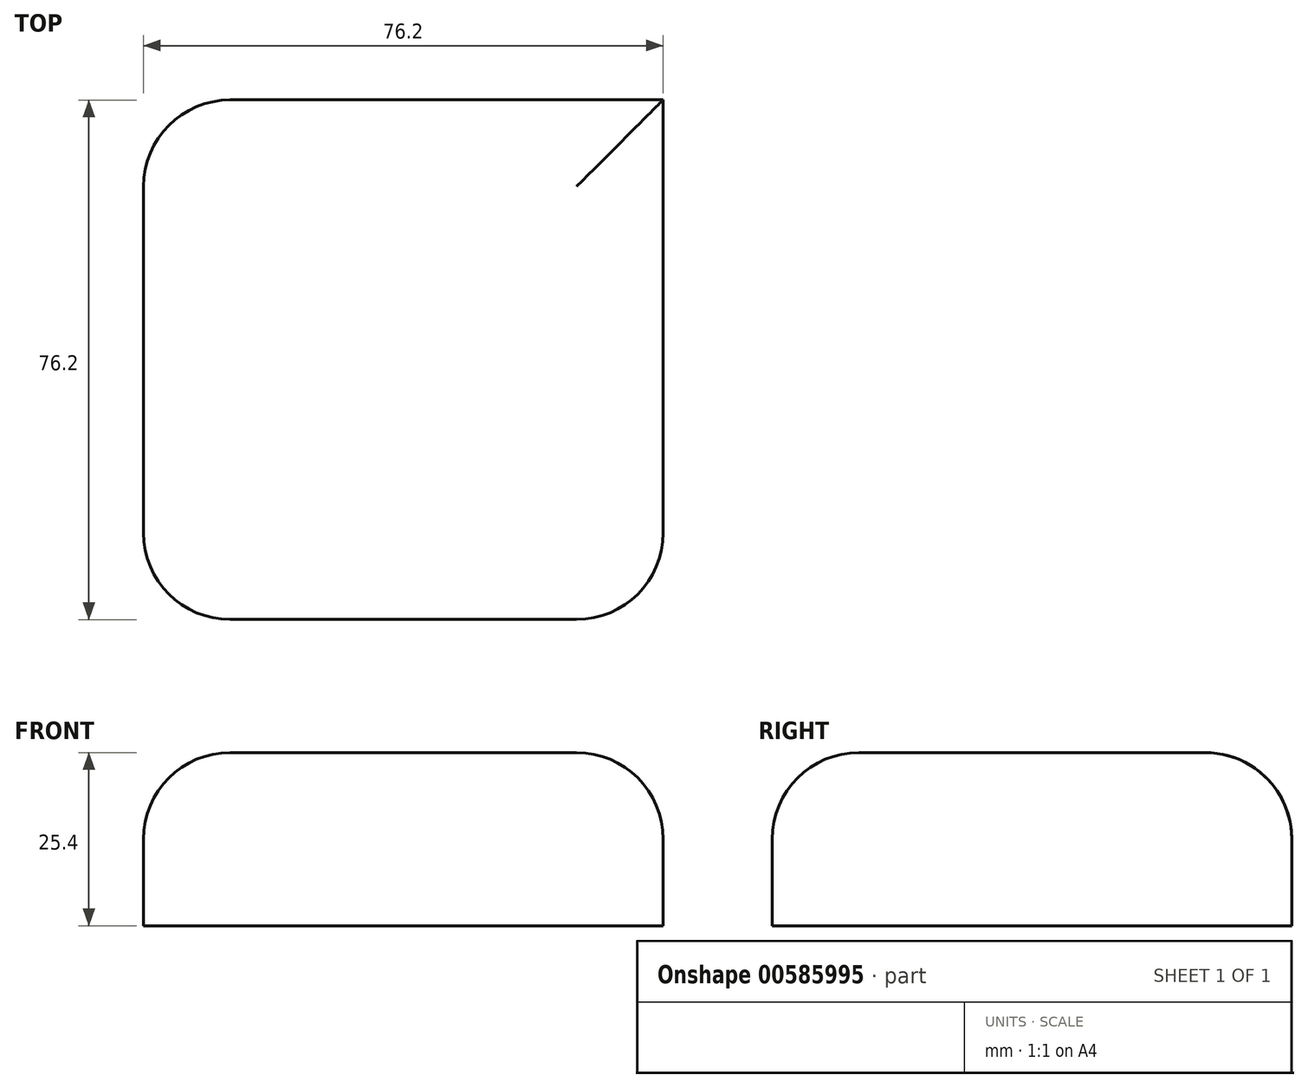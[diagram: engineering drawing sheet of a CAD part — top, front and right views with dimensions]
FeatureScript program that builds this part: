
annotation { "Feature Type Name" : "Feature", "Feature Type Description" : "" }
export const myFeature = defineFeature(function(context is Context, id is Id, definition is map)
    precondition{}
    {
        {
            var Q0;
            Q0=qCreatedBy(makeId("Top.planeOp"),FACE);
            var sketch = newSketch(context, id + "F0", { "sketchPlane" : qUnion([Q0])});
            skLineSegment(sketch, "E0.bottom", {"start": v(-38.8, 41.6) * mm, "end": v(37.4, 41.6) * mm});
            skLineSegment(sketch, "E0.top", {"start": v(-38.8, -34.6) * mm, "end": v(37.4, -34.6) * mm});
            skLineSegment(sketch, "E0.left", {"start": v(-38.8, 41.6) * mm, "end": v(-38.8, -34.6) * mm});
            skLineSegment(sketch, "E0.right", {"start": v(37.4, 41.6) * mm, "end": v(37.4, -34.6) * mm});
            skSolve(sketch);
        }
        {
            var Q0;
            Q0=makeQuery(id+"F0.imprint","IMPRINT",FACE,{"disambiguationData":[TD([[makeQuery(id+"F0.imprint","IMPRINT",EDGE,{"derivedFrom":sQuery(id+"F0.wireOp",EDGE,"E0.bottom")}),-1.0]])]});
            extrude(context, id + "F1", {"entities" : qUnion([Q0]), "depth" : 25.4 * mm, "offsetDistance" : 25.4 * mm});
        }
        {
            var Q0;
            Q0=makeQuery(id+"F1.opExtrude","SWEPT_EDGE",EDGE,{"disambiguationData":[OSD([sQuery(id+"F0.wireOp",EDGE,"E0.top"),sQuery(id+"F0.wireOp",EDGE,"E0.left")])]});
            var Q1;
            Q1=makeQuery(id+"F1.opExtrude","SWEPT_EDGE",EDGE,{"disambiguationData":[OSD([sQuery(id+"F0.wireOp",EDGE,"E0.top"),sQuery(id+"F0.wireOp",EDGE,"E0.right")])]});
            var Q2;
            Q2=makeQuery(id+"F1.opExtrude","SWEPT_EDGE",EDGE,{"disambiguationData":[OSD([sQuery(id+"F0.wireOp",EDGE,"E0.bottom"),sQuery(id+"F0.wireOp",EDGE,"E0.left")])]});
            var Q3;
            Q3=makeQuery(id+"F1.opExtrude","CAP_EDGE",EDGE,{"disambiguationData":[OSD([sQuery(id+"F0.wireOp",EDGE,"E0.left")])],"isStart":false});
            var Q4;
            Q4=makeQuery(id+"F1.opExtrude","CAP_EDGE",EDGE,{"disambiguationData":[OSD([sQuery(id+"F0.wireOp",EDGE,"E0.top")])],"isStart":false});
            var Q5;
            Q5=makeQuery(id+"F1.opExtrude","CAP_EDGE",EDGE,{"disambiguationData":[OSD([sQuery(id+"F0.wireOp",EDGE,"E0.right")])],"isStart":false});
            var Q6;
            Q6=makeQuery(id+"F1.opExtrude","CAP_EDGE",EDGE,{"disambiguationData":[OSD([sQuery(id+"F0.wireOp",EDGE,"E0.bottom")])],"isStart":false});
            fillet(context, id + "F2", {"entities" : qUnion([Q0, Q1, Q2, Q3, Q4, Q5, Q6]), "radius" : 12.7 * mm, "tangentPropagation" : true, "allowEdgeOverflow" : false});
        }
    });
